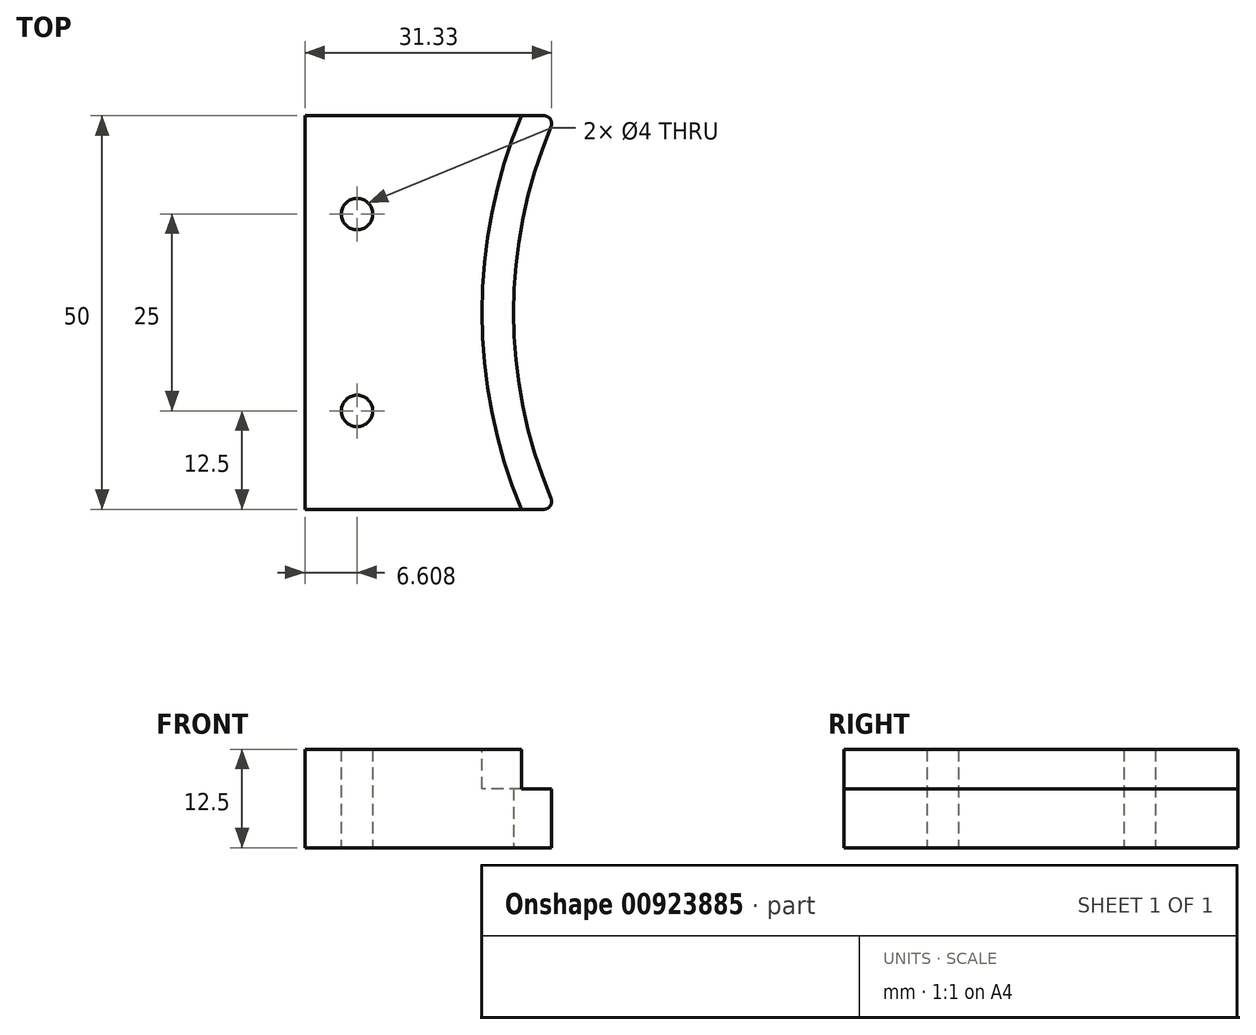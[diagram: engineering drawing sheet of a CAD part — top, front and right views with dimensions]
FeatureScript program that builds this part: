
annotation { "Feature Type Name" : "Feature", "Feature Type Description" : "" }
export const myFeature = defineFeature(function(context is Context, id is Id, definition is map)
    precondition{}
    {
        {
            var Q0;
            Q0=qCreatedBy(makeId("Top.planeOp"),FACE);
            var sketch = newSketch(context, id + "F0", { "sketchPlane" : qUnion([Q0])});
            skArc(sketch, "E0", {"start": v(-55.64, 25) * mm, "mid": v(-61, 0) * mm, "end": v(-55.64, -25) * mm});
            skLineSegment(sketch, "E1.bottom", {"start": v(-55.64, 25) * mm, "end": v(55.64, 25) * mm});
            skLineSegment(sketch, "E1.top", {"start": v(-55.64, -25) * mm, "end": v(55.64, -25) * mm});
            skLineSegment(sketch, "E1.left", {"start": v(-55.64, 25) * mm, "end": v(-55.64, -25) * mm});
            skLineSegment(sketch, "E1.right", {"start": v(55.64, 25) * mm, "end": v(55.64, -25) * mm});
            skLineSegment(sketch, "E2.bottom", {"start": v(-55.64, -25) * mm, "end": v(-88.14, -25) * mm});
            skLineSegment(sketch, "E2.top", {"start": v(-55.64, 25) * mm, "end": v(-88.14, 25) * mm});
            skLineSegment(sketch, "E2.left", {"start": v(-55.64, -25) * mm, "end": v(-55.64, 25) * mm});
            skLineSegment(sketch, "E2.right", {"start": v(-88.14, -25) * mm, "end": v(-88.14, 25) * mm});
            skLineSegment(sketch, "E3", {"start": v(-61, 25) * mm, "end": v(-61, -25) * mm});
            skArc(sketch, "E4.trimOffspring", {"start": v(55.64, -25) * mm, "mid": v(61, 0) * mm, "end": v(55.64, 25) * mm});
            skLineSegment(sketch, "E5", {"start": v(-61, 25) * mm, "end": v(-61, 23.5) * mm, "construction": true});
            skLineSegment(sketch, "E6", {"start": v(-61, 25) * mm, "end": v(-59.5, 25) * mm, "construction": true});
            skLineSegment(sketch, "E7", {"start": v(-59.5, 23.5) * mm, "end": v(-59.5, 19.13) * mm});
            skLineSegment(sketch, "E8", {"start": v(-59.5, 23.5) * mm, "end": v(-57.91, 23.5) * mm});
            skArc(sketch, "E9.trimOffspring", {"start": v(-57.91, 23.5) * mm, "mid": v(-58.75, 21.33) * mm, "end": v(-59.5, 19.13) * mm});
            skLineSegment(sketch, "E10.bottom", {"start": v(-88.14, 25) * mm, "end": v(-80.9, 25) * mm, "construction": true});
            skLineSegment(sketch, "E10.top", {"start": v(-88.14, 17.5) * mm, "end": v(-80.9, 17.5) * mm, "construction": true});
            skLineSegment(sketch, "E10.left", {"start": v(-88.14, 25) * mm, "end": v(-88.14, 17.5) * mm, "construction": true});
            skLineSegment(sketch, "E10.right", {"start": v(-80.9, 25) * mm, "end": v(-80.9, 17.5) * mm, "construction": true});
            skLineSegment(sketch, "E11.bottom", {"start": v(-88.14, 0) * mm, "end": v(-80.9, 0) * mm, "construction": true});
            skLineSegment(sketch, "E11.top", {"start": v(-88.14, 7.5) * mm, "end": v(-80.9, 7.5) * mm, "construction": true});
            skLineSegment(sketch, "E11.left", {"start": v(-88.14, 0) * mm, "end": v(-88.14, 7.5) * mm, "construction": true});
            skLineSegment(sketch, "E11.right", {"start": v(-80.9, 0) * mm, "end": v(-80.9, 7.5) * mm, "construction": true});
            skLineSegment(sketch, "E12", {"start": v(-88.14, 0) * mm, "end": v(-61, 0) * mm});
            skLineSegment(sketch, "E13.MirrorCS", {"start": v(-59.5, -23.5) * mm, "end": v(-59.5, -19.13) * mm});
            skLineSegment(sketch, "E14.MirrorCS", {"start": v(-59.5, -23.5) * mm, "end": v(-57.91, -23.5) * mm});
            skArc(sketch, "E15.MirrorCS", {"start": v(-57.91, -23.5) * mm, "mid": v(-58.75, -21.33) * mm, "end": v(-59.5, -19.13) * mm});
            skLineSegment(sketch, "E16", {"start": v(-80.9, 17.5) * mm, "end": v(-80.9, 7.5) * mm, "construction": true});
            skCircle(sketch, "E17", {"center": v(-80.9, 12.5) * mm, "radius": 2 * mm});
            skCircle(sketch, "E18.MirrorC", {"center": v(-80.9, -12.5) * mm, "radius": 2 * mm});
            skSolve(sketch);
        }
        {
            var Q0;
            Q0=qCreatedBy(makeId("Front.planeOp"),FACE);
            var sketch = newSketch(context, id + "F1", { "sketchPlane" : qUnion([Q0])});
            skLineSegment(sketch, "E19", {"start": v(-61, 0) * mm, "end": v(-61, 12.5) * mm, "construction": true});
            skLineSegment(sketch, "E20.bottom", {"start": v(-65, 7.5) * mm, "end": v(-57, 7.5) * mm});
            skLineSegment(sketch, "E20.top", {"start": v(-65, 17.5) * mm, "end": v(-57, 17.5) * mm});
            skLineSegment(sketch, "E20.left", {"start": v(-65, 7.5) * mm, "end": v(-65, 17.5) * mm});
            skLineSegment(sketch, "E20.right", {"start": v(-57, 7.5) * mm, "end": v(-57, 17.5) * mm});
            skPoint(sketch, "E20.middle", {"position": v(-61, 12.5) * mm});
            skLineSegment(sketch, "E21", {"start": v(0, 0) * mm, "end": v(0, 30.4) * mm, "construction": true});
            skSolve(sketch);
        }
        {
            var Q0;
            Q0=makeQuery(id+"F0.imprint","IMPRINT",FACE,{"disambiguationData":[TD([[makeQuery(id+"F0.imprint","IMPRINT",EDGE,{"derivedFrom":sQuery(id+"F0.wireOp",EDGE,"E7")}),-1.0]])]});
            var Q1;
            Q1=makeQuery(id+"F0.imprint","IMPRINT",FACE,{"disambiguationData":[TD([[makeQuery(id+"F0.imprint","IMPRINT",EDGE,{"derivedFrom":sQuery(id+"F0.wireOp",EDGE,"E13.MirrorCS")}),1.0]])]});
            var Q2;
            {var subQ3=sQuery(id+"F0.wireOp",EDGE,"E12");Q2=makeQuery(id+"F0.imprint","IMPRINT",FACE,{"disambiguationData":[TD([[makeQuery(id+"F0.imprint","IMPRINT",EDGE,{"derivedFrom":subQ3}),-1.0]])]});}
            var Q3;
            Q3=makeQuery(id+"F0.imprint","IMPRINT",FACE,{"disambiguationData":[TD([[makeQuery(id+"F0.imprint","IMPRINT",EDGE,{"derivedFrom":sQuery(id+"F0.wireOp",EDGE,"PVW8i8Wt-0xkI-O4RV-OvAW-XAR8i21FIH9G")}),-1.0]])]});
            var Q4;
            {var subQ3=sQuery(id+"F0.wireOp",EDGE,"E12");Q4=makeQuery(id+"F0.imprint","IMPRINT",FACE,{"disambiguationData":[TD([[makeQuery(id+"F0.imprint","IMPRINT",EDGE,{"derivedFrom":subQ3}),1.0]])]});}
            var Q5;
            Q5=makeQuery(id+"F0.imprint","IMPRINT",FACE,{"disambiguationData":[TD([[makeQuery(id+"F0.imprint","IMPRINT",EDGE,{"derivedFrom":sQuery(id+"F0.wireOp",EDGE,"E7")}),1.0]])]});
            var Q6;
            Q6=makeQuery(id+"F0.imprint","IMPRINT",FACE,{"disambiguationData":[TD([[makeQuery(id+"F0.imprint","IMPRINT",EDGE,{"derivedFrom":sQuery(id+"F0.wireOp",EDGE,"E13.MirrorCS")}),-1.0]])]});
            extrude(context, id + "F2", {"entities" : qUnion([Q0, Q1, Q2, Q3, Q4, Q5, Q6]), "depth" : 25 * mm, "offsetDistance" : 25 * mm});
        }
        {
            var Q0;
            Q0=makeQuery(id+"F1.imprint","IMPRINT",FACE,{"disambiguationData":[TD([[makeQuery(id+"F1.imprint","IMPRINT",EDGE,{"derivedFrom":sQuery(id+"F1.wireOp",EDGE,"E20.bottom")}),1.0]])]});
            var Q1;
            Q1=sQuery(id+"F1.wireOp",EDGE,"E21");
            revolve(context, id + "F3", {"operationType" : NewBodyOperationType.REMOVE, "surfaceOperationType" : NewSurfaceOperationType.NEW, "entities" : qUnion([Q0]), "axis" : qUnion([Q1]), "revolveType" : RevolveType.FULL, "oppositeDirection" : true});
        }
        {
            var Q0;
            {var subQ0=sQuery(id+"F0.wireOp",EDGE,"E0");var subQ1=sQuery(id+"F0.wireOp",EDGE,"E2.top");Q0=makeQuery(id+"F3.boolean.opBoolean","SPLIT",EDGE,{"disambiguationData":[TD([makeQuery(id+"F3.opRevolve","SWEPT_FACE",FACE,{"disambiguationData":[OSD([sQuery(id+"F1.wireOp",EDGE,"E20.top")])]})])],"derivedFrom":makeQuery(id+"F2.opExtrude","SWEPT_EDGE",EDGE,{"disambiguationData":[OSD([subQ0,sQuery(id+"F0.wireOp",EDGE,"E1.bottom"),subQ1,sQuery(id+"F0.wireOp",EDGE,"E2.left")])]})});}
            var Q1;
            {var subQ0=sQuery(id+"F0.wireOp",EDGE,"E0");var subQ1=sQuery(id+"F0.wireOp",EDGE,"E2.top");Q1=makeQuery(id+"F3.boolean.opBoolean","SPLIT",EDGE,{"disambiguationData":[TD([makeQuery(id+"F3.opRevolve","SWEPT_FACE",FACE,{"disambiguationData":[OSD([sQuery(id+"F1.wireOp",EDGE,"E20.bottom")])]})])],"derivedFrom":makeQuery(id+"F2.opExtrude","SWEPT_EDGE",EDGE,{"disambiguationData":[OSD([subQ0,sQuery(id+"F0.wireOp",EDGE,"E1.bottom"),subQ1,sQuery(id+"F0.wireOp",EDGE,"E2.left")])]})});}
            var Q2;
            {var subQ0=sQuery(id+"F0.wireOp",EDGE,"E0");var subQ1=sQuery(id+"F0.wireOp",EDGE,"E2.bottom");Q2=makeQuery(id+"F3.boolean.opBoolean","SPLIT",EDGE,{"disambiguationData":[TD([makeQuery(id+"F3.opRevolve","SWEPT_FACE",FACE,{"disambiguationData":[OSD([sQuery(id+"F1.wireOp",EDGE,"E20.bottom")])]})])],"derivedFrom":makeQuery(id+"F2.opExtrude","SWEPT_EDGE",EDGE,{"disambiguationData":[OSD([subQ0,sQuery(id+"F0.wireOp",EDGE,"E1.top"),subQ1,sQuery(id+"F0.wireOp",EDGE,"E2.left")])]})});}
            var Q3;
            {var subQ0=sQuery(id+"F0.wireOp",EDGE,"E0");var subQ1=sQuery(id+"F0.wireOp",EDGE,"E2.bottom");Q3=makeQuery(id+"F3.boolean.opBoolean","SPLIT",EDGE,{"disambiguationData":[TD([makeQuery(id+"F3.opRevolve","SWEPT_FACE",FACE,{"disambiguationData":[OSD([sQuery(id+"F1.wireOp",EDGE,"E20.top")])]})])],"derivedFrom":makeQuery(id+"F2.opExtrude","SWEPT_EDGE",EDGE,{"disambiguationData":[OSD([subQ0,sQuery(id+"F0.wireOp",EDGE,"E1.top"),subQ1,sQuery(id+"F0.wireOp",EDGE,"E2.left")])]})});}
            fillet(context, id + "F4", {"entities" : qUnion([Q0, Q1, Q2, Q3]), "radius" : 1 * mm, "tangentPropagation" : true, "allowEdgeOverflow" : false});
        }
        {
            var Q0;
            Q0=qCreatedBy(makeId("Front.planeOp"),FACE);
            var sketch = newSketch(context, id + "F5", { "sketchPlane" : qUnion([Q0])});
            skLineSegment(sketch, "E22.bottom", {"start": v(-87.5, 12.5) * mm, "end": v(87.5, 12.5) * mm});
            skLineSegment(sketch, "E22.top", {"start": v(-87.5, -12.5) * mm, "end": v(87.5, -12.5) * mm});
            skLineSegment(sketch, "E22.left", {"start": v(-87.5, 12.5) * mm, "end": v(-87.5, -12.5) * mm});
            skLineSegment(sketch, "E22.right", {"start": v(87.5, 12.5) * mm, "end": v(87.5, -12.5) * mm});
            skPoint(sketch, "E22.middle", {"position": v(0, 0) * mm});
            skSolve(sketch);
        }
        {
            var Q0;
            Q0 = qSketchRegion(id + "F5", true);
            extrude(context, id + "F6", {"entities" : qUnion([Q0]), "operationType" : NewBodyOperationType.INTERSECT, "endBound" : BoundingType.SYMMETRIC, "oppositeDirection" : true, "depth" : 50 * mm, "offsetDistance" : 25 * mm});
        }
    });
